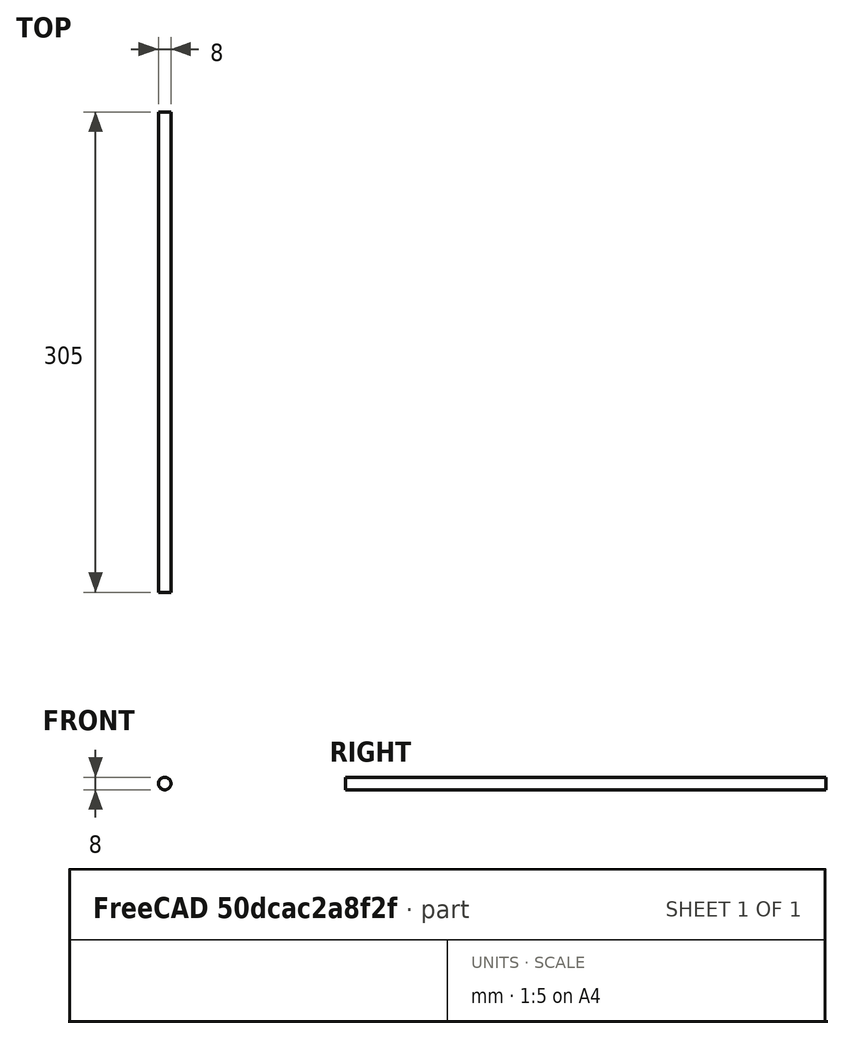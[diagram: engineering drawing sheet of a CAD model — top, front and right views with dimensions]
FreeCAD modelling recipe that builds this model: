
FCSTD DOCUMENT  (FreeCAD 0.19R21938 (Git))
Label: smoothrod-305mm
License: All rights reserved
LicenseURL: http://en.wikipedia.org/wiki/All_rights_reserved
objects: Sketcher::SketchObject×1, PartDesign::Pad×1, PartDesign::Body×1
note: 4 computed .brp shape members not serialized (recipe doc carries the construction recipe); baked Part::Feature solids carry a one-line shape summary decoded from their .brp

FEATURE [Sketcher::SketchObject] Sketch
  MapMode = 5
  Placement = pos=(0,0,0) rot=(1,0,0;1.5708rad)
  Support = -> [XZ_Plane]
  sketch-geometry (1):
    g0: Circle CenterX=0 CenterY=0 CenterZ=0 NormalX=0 NormalY=0 NormalZ=1 AngleXU=0 Radius=4
  constraints (2):
    c: Diameter(g0) = 8
    c: Coincident(g0,g-1)
FEATURE [PartDesign::Pad] Pad
  AllowMultiFace = false
  Length = 305
  Length2 = 100
  Placement = pos=(0,0,0) rot=(1,0,0;1.5708rad)
  Profile = -> Sketch
  Type = 0
FEATURE [PartDesign::Body] Body  label="smoothrod-305mm"
  Group = -> [Sketch,Pad]
  Origin = -> Origin
  Tip = -> Pad
